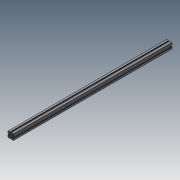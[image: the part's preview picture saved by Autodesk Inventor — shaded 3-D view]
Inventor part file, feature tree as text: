
AUTODESK INVENTOR PART (.ipt)
format: ipt  version: 2018.3 (Build 223284000, 284)  size: 236,032 bytes
history: native  units: in
note: dims shown in document units (in); Inventor stores cm internally (conversion verified against a paired STEP export)
features: extrude x1, sketch x1, projected_geometry x1
ambient origin geometry x8: Origin, YZ Plane, XZ Plane, XY Plane, X Axis, Y Axis, Z Axis, Center Point
bodies: Body1 (feature_tree)
feature tree (3):
  extrude  "Extrusion1"  [1 undecoded]
  sketch  "Sketch1"  dims[d0=42.0in d1=0.0in]
  projected_geometry  "Projected Loop1"
note: 1 required parameter value undecoded (feature->parameter linkage not recoverable at this tier; creation-order binding heuristic only, values carry confidence <= 0.55)
